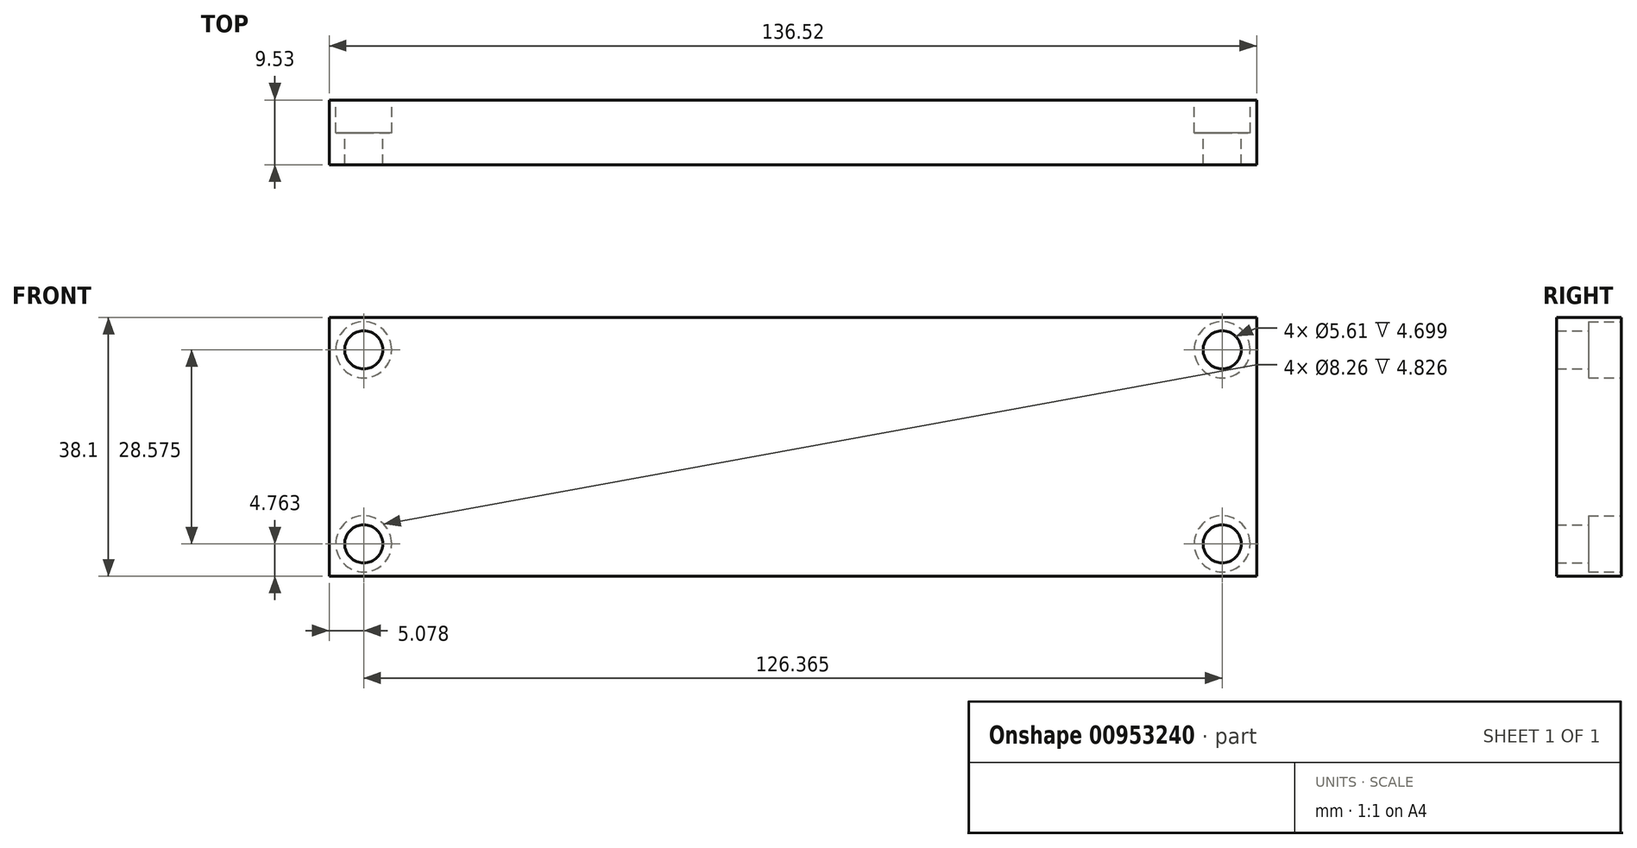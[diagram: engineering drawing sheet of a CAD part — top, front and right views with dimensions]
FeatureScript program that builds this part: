
annotation { "Feature Type Name" : "Feature", "Feature Type Description" : "" }
export const myFeature = defineFeature(function(context is Context, id is Id, definition is map)
    precondition{}
    {
        {
            var Q0;
            Q0=qCreatedBy(makeId("Front.planeOp"),FACE);
            var sketch = newSketch(context, id + "F0", { "sketchPlane" : qUnion([Q0])});
            skLineSegment(sketch, "E0.bottom", {"start": v(-68.26, 19.05) * mm, "end": v(30.16, 19.05) * mm});
            skLineSegment(sketch, "E0.top", {"start": v(-68.26, -19.05) * mm, "end": v(68.26, -19.05) * mm});
            skLineSegment(sketch, "E0.left", {"start": v(-68.26, 19.05) * mm, "end": v(-68.26, -19.05) * mm});
            skLineSegment(sketch, "E0.right", {"start": v(68.26, 19.05) * mm, "end": v(68.26, -19.05) * mm});
            skPoint(sketch, "E0.middle", {"position": v(0, 0) * mm});
            skLineSegment(sketch, "E1.trimOffspring", {"start": v(30.16, 19.05) * mm, "end": v(68.26, 19.05) * mm});
            skPoint(sketch, "E2", {"position": v(-63.18, 14.29) * mm});
            skPoint(sketch, "E3", {"position": v(63.18, 14.29) * mm});
            skPoint(sketch, "E4", {"position": v(63.18, -14.29) * mm});
            skPoint(sketch, "E5", {"position": v(-63.18, -14.29) * mm});
            skPoint(sketch, "E6.orphan", {"position": v(-30.16, 19.05) * mm});
            skSolve(sketch);
        }
        {
            var Q0;
            Q0=makeQuery(id+"F0.imprint","IMPRINT",FACE,{"disambiguationData":[TD([[makeQuery(id+"F0.imprint","IMPRINT",EDGE,{"derivedFrom":sQuery(id+"F0.wireOp",EDGE,"E0.bottom")}),-1.0]])]});
            extrude(context, id + "F1", {"entities" : qUnion([Q0]), "depth" : 9.52 * mm, "offsetDistance" : 25.4 * mm});
        }
        {
            var Q0;
            Q0=sQuery(id+"F0.wireOp",VERTEX,"E2");
            var Q1;
            Q1=sQuery(id+"F0.wireOp",VERTEX,"E5");
            var Q2;
            Q2=sQuery(id+"F0.wireOp",VERTEX,"E4");
            var Q3;
            Q3=sQuery(id+"F0.wireOp",VERTEX,"E3");
            var Q4;
            Q4=makeQuery(id+"F1.opExtrude","SWEPT_BODY",BODY,{"disambiguationData":[OSD([sQuery(id+"F0.wireOp",EDGE,"E0.bottom"),sQuery(id+"F0.wireOp",EDGE,"E0.top"),sQuery(id+"F0.wireOp",EDGE,"E0.left"),sQuery(id+"F0.wireOp",EDGE,"E0.right"),sQuery(id+"F0.wireOp",EDGE,"nqivvyWs-Tsi8-Vpzt-1zEC-vecyQ78LZCim"),sQuery(id+"F0.wireOp",EDGE,"lamHV6p6-MYJ2-S0ze-Kp3E-AKDUZ7zqxq5T"),sQuery(id+"F0.wireOp",EDGE,"JGdL0lD0-H8CL-dosD-QgfF-y8SBXPBlDuZD"),sQuery(id+"F0.wireOp",EDGE,"E1.trimOffspring")])]});
            hole(context, id + "F2", {"style" : HoleStyle.C_BORE, "endStyle" : HoleEndStyle.BLIND, "oppositeDirection" : true, "holeDiameter" : 5.61 * mm, "cBoreDiameter" : 8.25 * mm, "cBoreDepth" : 4.83 * mm, "majorDiameter" : 6.35 * mm, "holeDepth" : 9.52 * mm, "tappedDepth" : 20.33 * mm, "tapClearance" : 3, "locations" : qUnion([Q0, Q1, Q2, Q3]), "scope" : qUnion([Q4])});
        }
    });
